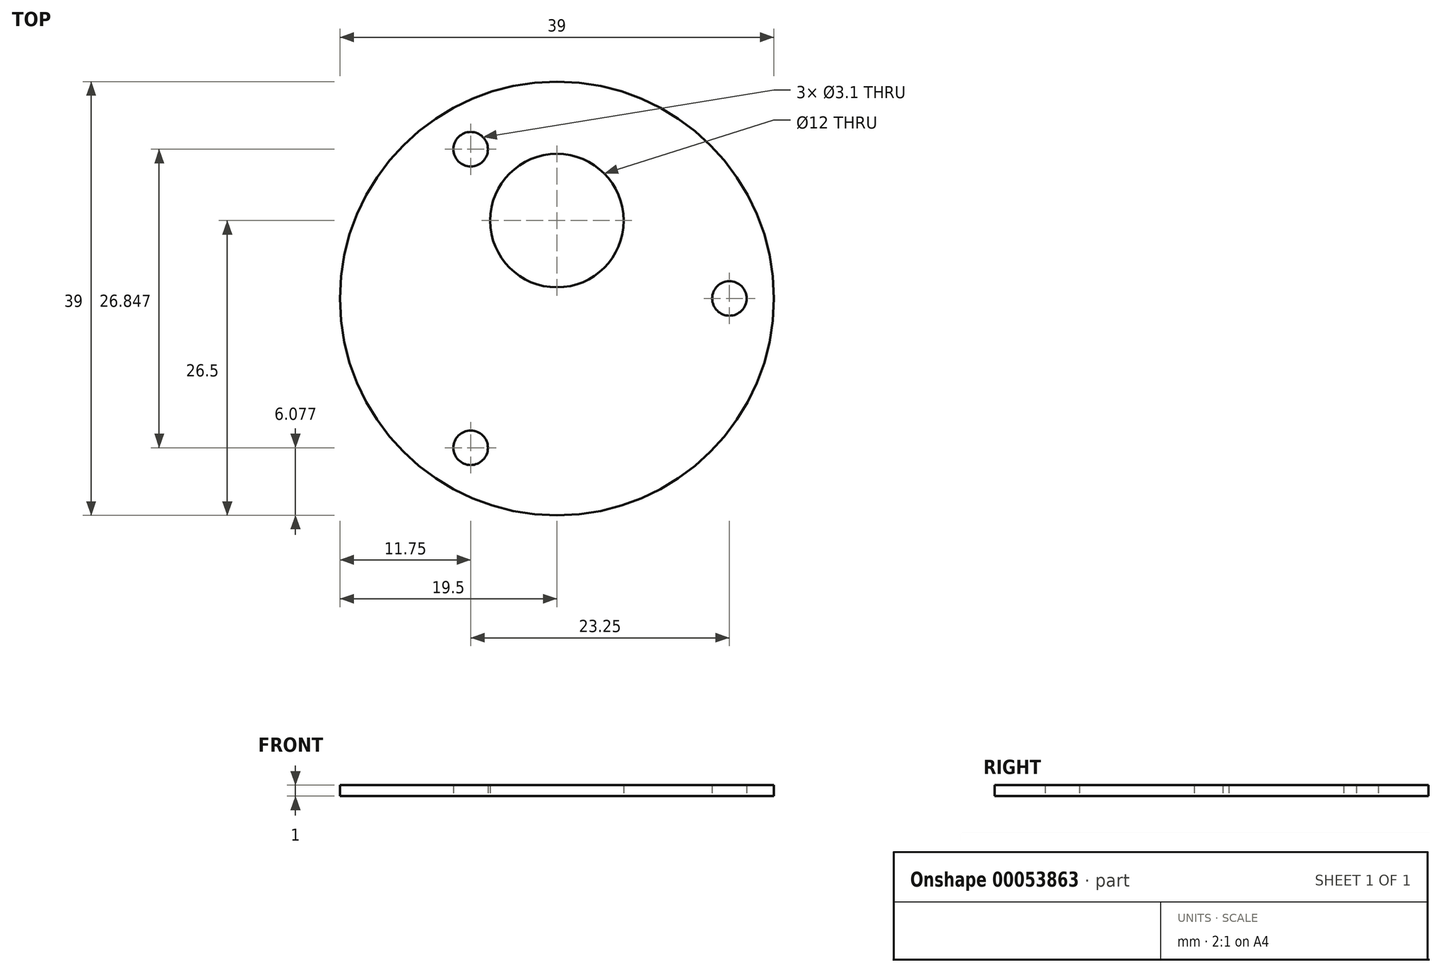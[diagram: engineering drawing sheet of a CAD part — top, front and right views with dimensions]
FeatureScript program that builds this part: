
annotation { "Feature Type Name" : "Feature", "Feature Type Description" : "" }
export const myFeature = defineFeature(function(context is Context, id is Id, definition is map)
    precondition{}
    {
        {
            var Q0;
            Q0=qCreatedBy(makeId("Top.planeOp"),FACE);
            var sketch = newSketch(context, id + "F0", { "sketchPlane" : qUnion([Q0])});
            skCircle(sketch, "E0.cCircle", {"center": v(0, 0) * mm, "radius": 15.5 * mm, "construction": true});
            skLineSegment(sketch, "E0.0", {"start": v(15.5, 0) * mm, "end": v(-7.75, -13.42) * mm, "construction": true});
            skLineSegment(sketch, "E0.1", {"start": v(-7.75, -13.42) * mm, "end": v(-7.75, 13.42) * mm, "construction": true});
            skLineSegment(sketch, "E0.2", {"start": v(-7.75, 13.42) * mm, "end": v(15.5, 0) * mm, "construction": true});
            skCircle(sketch, "E1", {"center": v(-7.75, 13.42) * mm, "radius": 1.55 * mm});
            skCircle(sketch, "E2", {"center": v(15.5, 0) * mm, "radius": 1.55 * mm});
            skCircle(sketch, "E3", {"center": v(-7.75, -13.42) * mm, "radius": 1.55 * mm});
            skCircle(sketch, "E4", {"center": v(0, 7) * mm, "radius": 6 * mm});
            skCircle(sketch, "E5", {"center": v(0, 0) * mm, "radius": 19.5 * mm});
            skSolve(sketch);
        }
        {
            var Q0;
            Q0 = qSketchRegion(id + "F0", true);
            extrude(context, id + "F1", {"entities" : qUnion([Q0]), "depth" : 1 * mm});
        }
    });
